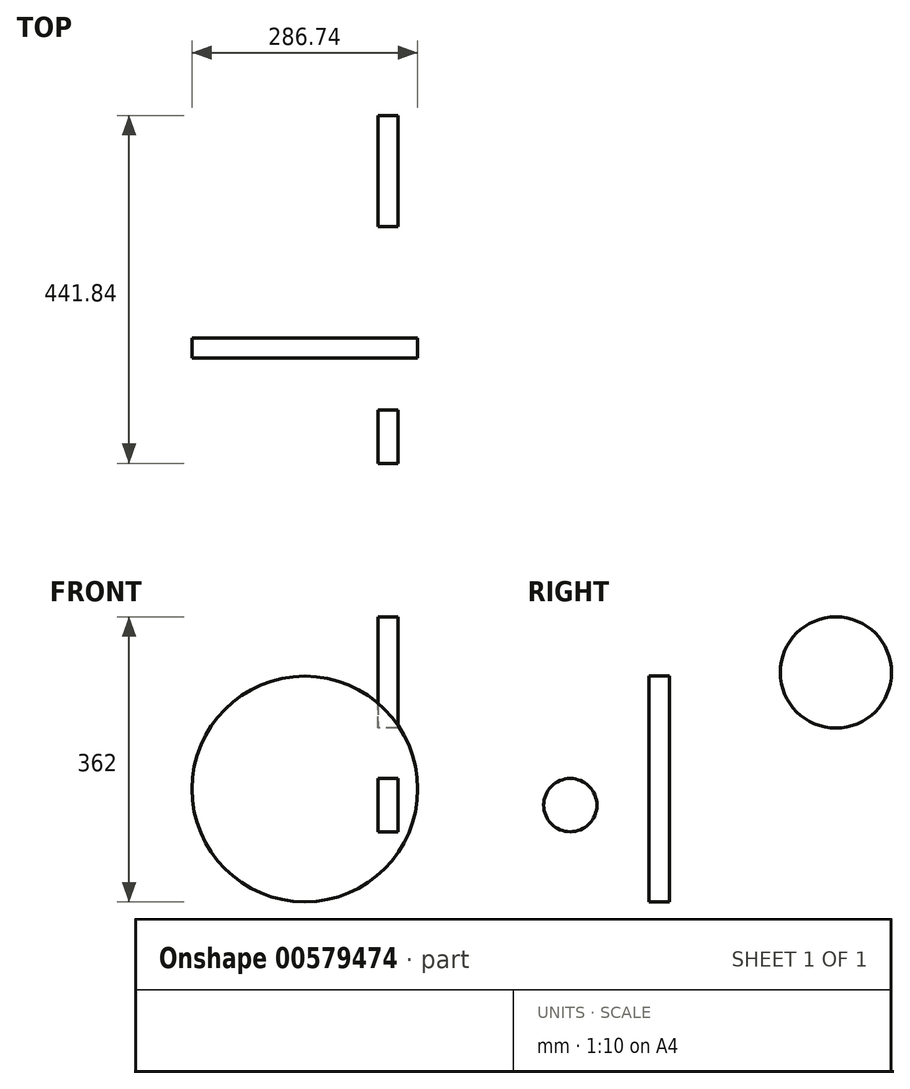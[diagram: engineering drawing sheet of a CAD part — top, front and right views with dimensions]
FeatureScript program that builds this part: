
annotation { "Feature Type Name" : "Feature", "Feature Type Description" : "" }
export const myFeature = defineFeature(function(context is Context, id is Id, definition is map)
    precondition{}
    {
        {
            var Q0;
            Q0=qCreatedBy(makeId("Right.planeOp"),FACE);
            var sketch = newSketch(context, id + "F0", { "sketchPlane" : qUnion([Q0])});
            skCircle(sketch, "E0", {"center": v(-125.7, 66.52) * mm, "radius": 33.83 * mm});
            skSolve(sketch);
        }
        {
            var Q0;
            Q0=makeQuery(id+"F0.imprint","IMPRINT",FACE,{"disambiguationData":[TD([[makeQuery(id+"F0.imprint","IMPRINT",EDGE,{"derivedFrom":sQuery(id+"F0.wireOp",EDGE,"E0")}),1.0]])]});
            extrude(context, id + "F1", {"entities" : qUnion([Q0]), "depth" : 25.4 * mm, "offsetDistance" : 25.4 * mm});
        }
        {
            var Q0;
            Q0=qCreatedBy(makeId("Right.planeOp"),FACE);
            var sketch = newSketch(context, id + "F2", { "sketchPlane" : qUnion([Q0])});
            skCircle(sketch, "E1", {"center": v(211.71, 235.02) * mm, "radius": 70.6 * mm});
            skSolve(sketch);
        }
        {
            var Q0;
            Q0=makeQuery(id+"F2.imprint","IMPRINT",FACE,{"disambiguationData":[TD([[makeQuery(id+"F2.imprint","IMPRINT",EDGE,{"derivedFrom":sQuery(id+"F2.wireOp",EDGE,"E1")}),1.0]])]});
            extrude(context, id + "F3", {"entities" : qUnion([Q0]), "depth" : 25.4 * mm, "offsetDistance" : 25.4 * mm});
        }
        {
            var Q0;
            Q0=qCreatedBy(makeId("Front.planeOp"),FACE);
            var sketch = newSketch(context, id + "F4", { "sketchPlane" : qUnion([Q0])});
            skCircle(sketch, "E2", {"center": v(-92.93, 87) * mm, "radius": 143.37 * mm});
            skSolve(sketch);
        }
        {
            var Q0;
            Q0=makeQuery(id+"F4.imprint","IMPRINT",FACE,{"disambiguationData":[TD([[makeQuery(id+"F4.imprint","IMPRINT",EDGE,{"derivedFrom":sQuery(id+"F4.wireOp",EDGE,"E2")}),1.0]])]});
            extrude(context, id + "F5", {"entities" : qUnion([Q0]), "depth" : 25.4 * mm, "offsetDistance" : 25.4 * mm});
        }
    });
